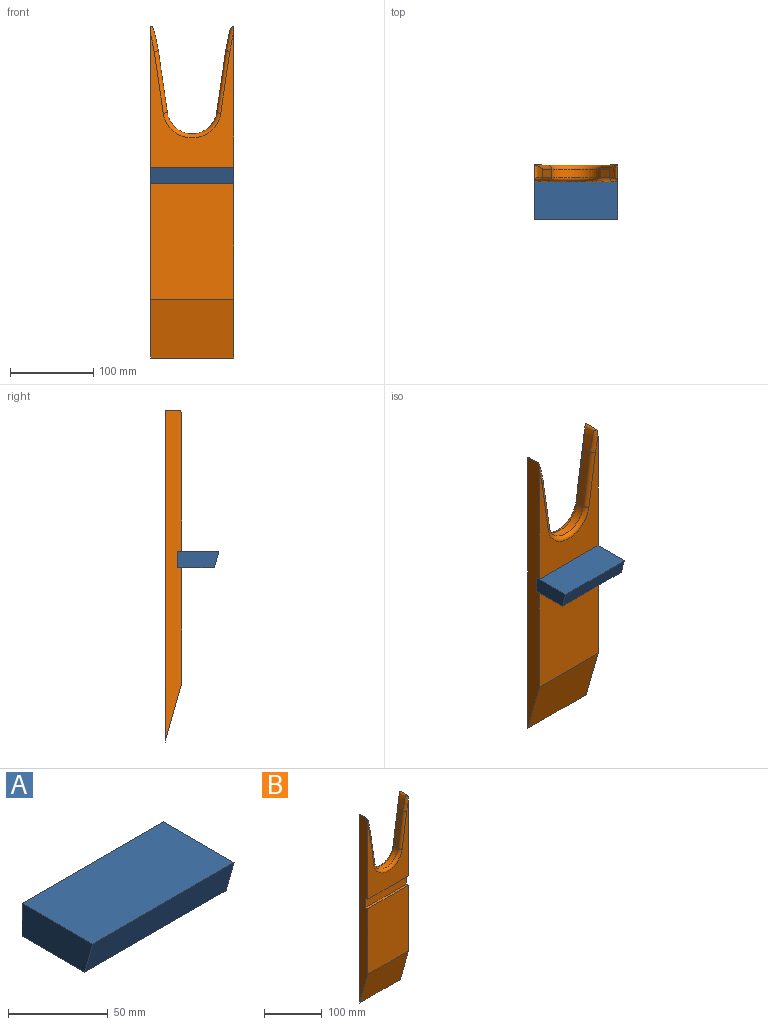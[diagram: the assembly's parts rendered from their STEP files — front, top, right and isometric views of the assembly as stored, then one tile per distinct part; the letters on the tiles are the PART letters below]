
ASSEMBLY  parts=2 mates=1
PART A: 6 faces, bbox 100x50x20 mm
  f0: plane 100x50mm, normal (0,0,1), area 5000mm2, adj f1,f3,f4,f5
  f1: plane 50x20mm, normal (-1,0,0), area 943.5mm2, adj f0,f2,f4,f5
  f2: plane 100x44.35mm, normal (0,0,-1), area 4434.8mm2, adj f1,f3,f4,f5
  f3: plane 50x20mm, normal (1,0,0), area 943.5mm2, adj f0,f2,f4,f5
  f4: plane 100x20mm, normal (0,1,0), area 2000mm2, adj f0,f1,f2,f3
  f5: plane 100x20mm, normal (0,-0.96,-0.27), area 2078.3mm2, adj f0,f1,f2,f3
PART B: 22 faces, bbox 109.5x20x402.7 mm
  f0: plane 160.76x100mm, normal (0,-1,0), area 6498.6mm2, adj f1,f3,f13,f14,f15,f16,f17,f18
  f1: plane 400x20mm, normal (-1,0,0), area 7187.9mm2, adj f0,f2,f8,f9,f10,f13,f18,f19
  f2: extruded ~29.8x18mm, area 410.4mm2, adj f1,f7,f10,f13
  f3: plane 400x20mm, normal (1,0,0), area 7187.9mm2, adj f0,f4,f8,f9,f11,f14,f18,f19
  f4: extruded ~29.8x18mm, area 410.4mm2, adj f3,f5,f11,f14
  f5: plane 74.55x10.94mm, normal (-0.99,0,0.15), area 753.5mm2, adj f4,f6,f11,f16
  f6: cylinder r=30mm len=59.36mm, axis (0,1,0), area 855mm2, adj f5,f7,f12,f17
  f7: plane 74.55x10.94mm, normal (0.99,0,0.15), area 753.5mm2, adj f2,f6,f10,f15
  f8: plane 139.23x100mm, normal (0,-1,0), area 13923.1mm2, adj f1,f3,f19,f21
  f9: plane 399.64x100mm, normal (0,1,0), area 29531.7mm2, adj f1,f3,f10,f11,f12,f21
  f10: cylinder r=5mm len=105.8mm, axis (-0.15,0,0.99), area 744.3mm2, adj f1,f2,f7,f9,f12
  f11: cylinder r=5mm len=105.8mm, axis (-0.15,0,-0.99), area 744.3mm2, adj f3,f4,f5,f9,f12
  f12: torus R=35mm, axis (0,-1,0), area 712.2mm2, adj f6,f9,f10,f11
  f13: bspline ~47.09x16.62mm, area 224.8mm2, adj f0,f1,f2,f15
  f14: bspline ~47.14x16.64mm, area 224.8mm2, adj f0,f3,f4,f16
  f15: cylinder r=5mm len=75.28mm, axis (0.15,0,-0.99), area 591.5mm2, adj f0,f7,f13,f17
  f16: cylinder r=5mm len=75.28mm, axis (0.15,0,0.99), area 591.5mm2, adj f0,f5,f14,f17
  f17: torus R=35mm, axis (0,-1,0), area 712.2mm2, adj f0,f6,f15,f16
  f18: plane 100x5mm, normal (0,0,-1), area 500mm2, adj f0,f1,f3,f20
  f19: plane 100x5mm, normal (0,0,1), area 500mm2, adj f1,f3,f8,f20
  f20: plane 100x20mm, normal (0,-1,0), area 2000mm2, adj f1,f3,f18,f19
  f21: plane 100x70.77mm, normal (0,-0.96,-0.27), area 7354.1mm2, adj f1,f3,f8,f9
PLACE A t=(-269.01,3.92,121.45)mm
PLACE B t=(-269.01,3.92,121.45)mm
MATE fastened B.f20 <-> A.f4  axis (0,-1,0) through (-219.01,-11.08,341.45)mm
